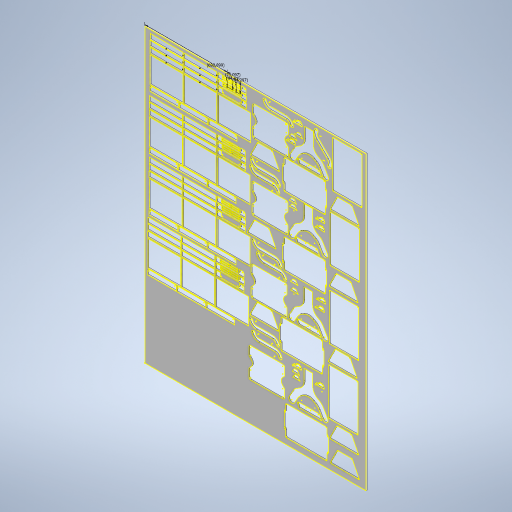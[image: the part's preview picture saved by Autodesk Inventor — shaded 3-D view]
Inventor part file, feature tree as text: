
AUTODESK INVENTOR PART (.ipt)
format: ipt  version: 2024 (Build 280153000, 153)  size: 3,638,784 bytes
history: native  units: mm
features: other x2, sketch x2, extrude x1, projected_geometry x1
ambient origin geometry x8: Origin, YZ Plane, XZ Plane, XY Plane, X Axis, Y Axis, Z Axis, Center Point
bodies: Body1 (feature_tree)
feature tree (6):
  other  "Sólido1"
  sketch  "Boceto1"  dims[d0=1850.0mm d1=2440.0mm]
  extrude  "Extrusión1"  Depth=2440.0mm
  sketch  "Boceto6"  dims[d2=10.0mm d3=0.0mm d52=94.43027mm d56=94.296686mm d60=690.898577mm d64=75.096659mm]
  other  "Visible"
  projected_geometry  "Contorno proyectado71"
